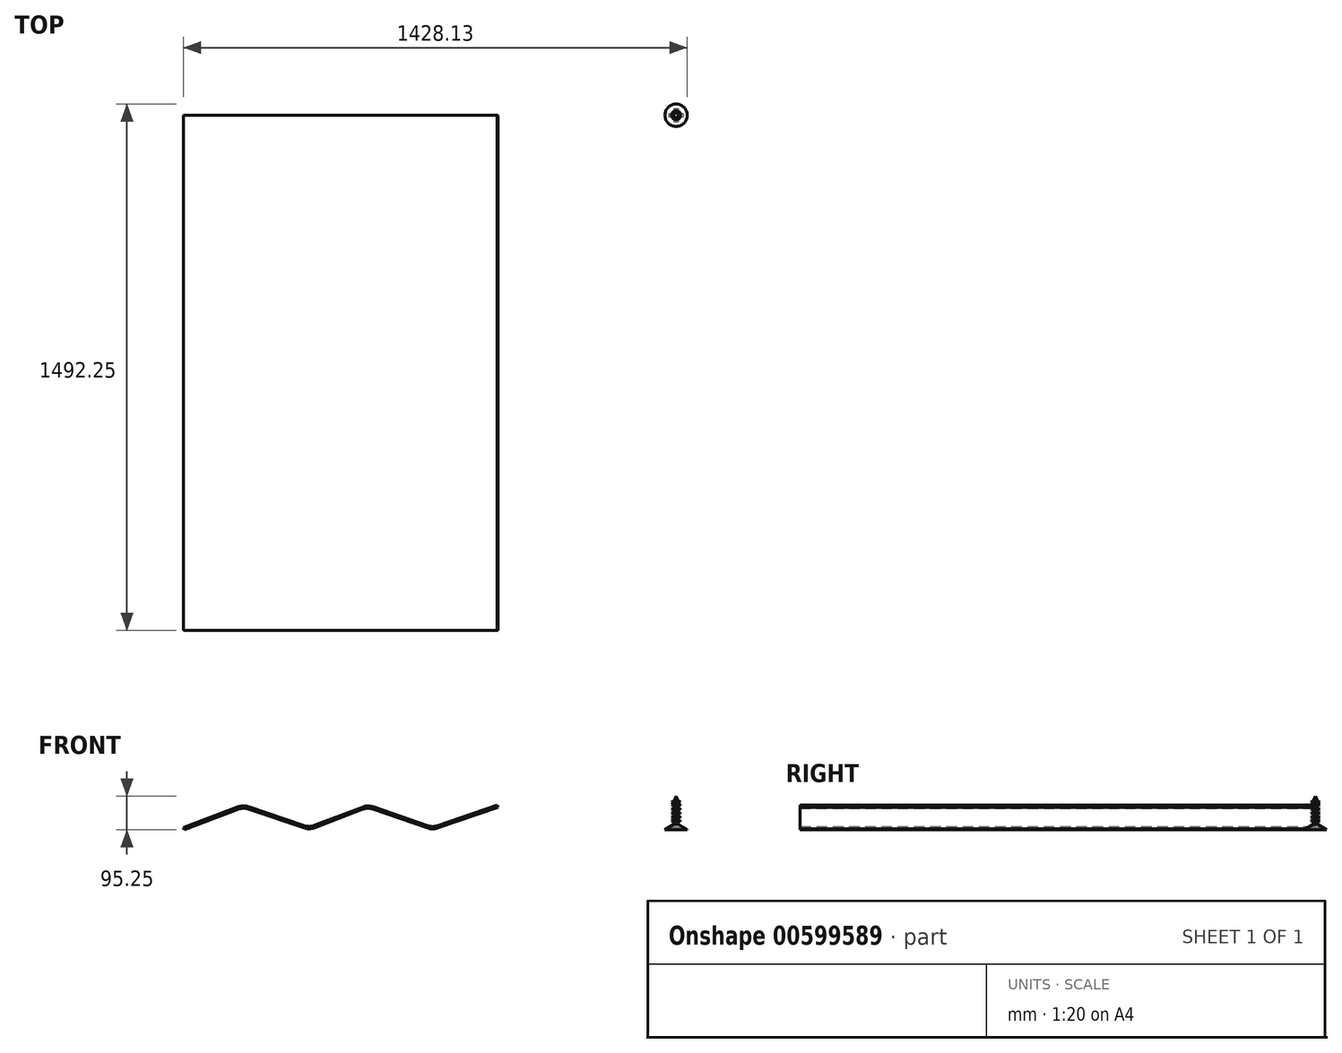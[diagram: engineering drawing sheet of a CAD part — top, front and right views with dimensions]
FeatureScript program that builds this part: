
annotation { "Feature Type Name" : "Feature", "Feature Type Description" : "" }
export const myFeature = defineFeature(function(context is Context, id is Id, definition is map)
    precondition{}
    {
        {
            var Q0;
            Q0=qCreatedBy(makeId("Front.planeOp"),FACE);
            var sketch = newSketch(context, id + "F0", { "sketchPlane" : qUnion([Q0])});
            skLineSegment(sketch, "E0", {"start": v(-278.83, 0) * mm, "end": v(-248.09, 11.64) * mm});
            skLineSegment(sketch, "E1", {"start": v(-242.43, 11.73) * mm, "end": v(-210.73, 0.97) * mm});
            skLineSegment(sketch, "E2", {"start": v(-205.03, 1.08) * mm, "end": v(-177.55, 11.6) * mm});
            skLineSegment(sketch, "E3", {"start": v(-171.8, 11.7) * mm, "end": v(-140.78, 0.95) * mm});
            skLineSegment(sketch, "E4", {"start": v(-135.32, 0.94) * mm, "end": v(-101.03, 12.7) * mm});
            skPoint(sketch, "E5.visualSharp", {"position": v(-245.28, 12.7) * mm});
            skArc(sketch, "E5.filletArc", {"start": v(-242.43, 11.73) * mm, "mid": v(-245.27, 12.18) * mm, "end": v(-248.09, 11.64) * mm});
            skPoint(sketch, "E6.visualSharp", {"position": v(-174.7, 12.7) * mm});
            skArc(sketch, "E6.filletArc", {"start": v(-171.8, 11.7) * mm, "mid": v(-174.69, 12.16) * mm, "end": v(-177.55, 11.6) * mm});
            skPoint(sketch, "E7.visualSharp", {"position": v(-138.05, 0) * mm});
            skArc(sketch, "E7.filletArc", {"start": v(-140.78, 0.95) * mm, "mid": v(-138.05, 0.48) * mm, "end": v(-135.32, 0.94) * mm});
            skPoint(sketch, "E8.visualSharp", {"position": v(-207.86, 0) * mm});
            skArc(sketch, "E8.filletArc", {"start": v(-210.73, 0.97) * mm, "mid": v(-207.87, 0.53) * mm, "end": v(-205.03, 1.08) * mm});
            skLineSegment(sketch, "E9.0", {"start": v(-135.32, 2.28) * mm, "end": v(-101.44, 13.9) * mm});
            skLineSegment(sketch, "E9.1", {"start": v(-171.4, 12.9) * mm, "end": v(-140.78, 2.29) * mm});
            skArc(sketch, "E9.2", {"start": v(-171.4, 12.9) * mm, "mid": v(-174.7, 13.43) * mm, "end": v(-178, 12.8) * mm});
            skLineSegment(sketch, "E9.3", {"start": v(-279.28, 1.19) * mm, "end": v(-248.54, 12.82) * mm});
            skArc(sketch, "E9.4", {"start": v(-242.02, 12.94) * mm, "mid": v(-245.29, 13.45) * mm, "end": v(-248.54, 12.82) * mm});
            skLineSegment(sketch, "E9.5", {"start": v(-242.02, 12.94) * mm, "end": v(-210.75, 2.32) * mm});
            skLineSegment(sketch, "E9.6", {"start": v(-205.06, 2.43) * mm, "end": v(-178, 12.8) * mm});
            skPoint(sketch, "E10.visualSharp", {"position": v(-207.89, 1.35) * mm});
            skArc(sketch, "E10.filletArc", {"start": v(-210.75, 2.32) * mm, "mid": v(-207.9, 1.88) * mm, "end": v(-205.06, 2.43) * mm});
            skPoint(sketch, "E11.visualSharp", {"position": v(-138.05, 1.34) * mm});
            skArc(sketch, "E11.filletArc", {"start": v(-140.78, 2.29) * mm, "mid": v(-138.05, 1.83) * mm, "end": v(-135.32, 2.28) * mm});
            skLineSegment(sketch, "E12", {"start": v(-101.03, 12.7) * mm, "end": v(-101.44, 13.9) * mm});
            skLineSegment(sketch, "E13", {"start": v(-278.83, 0) * mm, "end": v(-279.28, 1.19) * mm});
            skSolve(sketch);
        }
        {
            var Q0;
            Q0 = qSketchRegion(id + "F0", true);
            extrude(context, id + "F1", {"entities" : qUnion([Q0]), "depth" : 292.1 * mm, "offsetDistance" : 25.4 * mm});
        }
        {
            var Q0;
            Q0=qCreatedBy(makeId("Front.planeOp"),FACE);
            var sketch = newSketch(context, id + "F2", { "sketchPlane" : qUnion([Q0])});
            skLineSegment(sketch, "E14", {"start": v(0, 0) * mm, "end": v(-6.35, 0) * mm});
            skLineSegment(sketch, "E15", {"start": v(-6.35, 0) * mm, "end": v(-1.27, 2.96) * mm});
            skLineSegment(sketch, "E16", {"start": v(-1.27, 16.26) * mm, "end": v(0, 19.05) * mm});
            skLineSegment(sketch, "E17", {"start": v(-1.27, 2.96) * mm, "end": v(-1.27, 4.5) * mm});
            skLineSegment(sketch, "E18", {"start": v(-1.27, 4.5) * mm, "end": v(-2.54, 4.95) * mm});
            skLineSegment(sketch, "E19", {"start": v(-2.54, 4.95) * mm, "end": v(-1.27, 5.37) * mm});
            skLineSegment(sketch, "E20", {"start": v(-1.27, 5.37) * mm, "end": v(-1.27, 6.75) * mm});
            skLineSegment(sketch, "E21", {"start": v(-1.27, 6.75) * mm, "end": v(-2.54, 7.2) * mm});
            skLineSegment(sketch, "E22", {"start": v(-2.54, 7.2) * mm, "end": v(-1.27, 7.63) * mm});
            skLineSegment(sketch, "E23", {"start": v(-1.27, 7.63) * mm, "end": v(-1.27, 8.98) * mm});
            skLineSegment(sketch, "E24", {"start": v(-1.27, 8.98) * mm, "end": v(-2.54, 9.5) * mm});
            skLineSegment(sketch, "E25", {"start": v(-2.54, 9.5) * mm, "end": v(-1.27, 9.92) * mm});
            skLineSegment(sketch, "E26", {"start": v(-1.27, 9.92) * mm, "end": v(-1.27, 11.34) * mm});
            skLineSegment(sketch, "E27", {"start": v(-1.27, 11.34) * mm, "end": v(-2.54, 11.76) * mm});
            skLineSegment(sketch, "E28", {"start": v(-2.54, 11.76) * mm, "end": v(-1.27, 12.18) * mm});
            skLineSegment(sketch, "E29", {"start": v(-1.27, 12.18) * mm, "end": v(-1.27, 13.64) * mm});
            skLineSegment(sketch, "E30", {"start": v(-1.27, 13.64) * mm, "end": v(-2.54, 14.1) * mm});
            skLineSegment(sketch, "E31", {"start": v(-2.54, 14.1) * mm, "end": v(-1.27, 14.52) * mm});
            skLineSegment(sketch, "E32", {"start": v(-1.27, 14.52) * mm, "end": v(-1.27, 15.38) * mm});
            skLineSegment(sketch, "E33", {"start": v(-1.27, 15.38) * mm, "end": v(-2.54, 15.76) * mm});
            skLineSegment(sketch, "E34", {"start": v(-2.54, 15.76) * mm, "end": v(-1.27, 16.26) * mm});
            skPoint(sketch, "E35", {"position": v(-1.27, 10.63) * mm});
            skLineSegment(sketch, "E36", {"start": v(-3.4, 10.63) * mm, "end": v(3.08, 10.63) * mm, "construction": true});
            skLineSegment(sketch, "E37", {"start": v(0, 19.05) * mm, "end": v(0, 0) * mm});
            skSolve(sketch);
        }
        {
            var Q0;
            Q0=makeQuery(id+"F2.imprint","IMPRINT",FACE,{"disambiguationData":[TD([[makeQuery(id+"F2.imprint","IMPRINT",EDGE,{"derivedFrom":sQuery(id+"F2.wireOp",EDGE,"E14")}),-1.0]])]});
            var Q1;
            Q1=sQuery(id+"F2.wireOp",EDGE,"E37");
            revolve(context, id + "F3", {"entities" : qUnion([Q0]), "axis" : qUnion([Q1]), "revolveType" : RevolveType.FULL});
        }
        {
            var Q0;
            Q0=makeQuery(id+"F3.opRevolve","SWEPT_FACE",FACE,{"disambiguationData":[OSD([sQuery(id+"F2.wireOp",EDGE,"E14")])]});
            var sketch = newSketch(context, id + "F4", { "sketchPlane" : qUnion([Q0])});
            skLineSegment(sketch, "E38", {"start": v(-1.04, 3.9) * mm, "end": v(-1.04, 1.01) * mm});
            skLineSegment(sketch, "E39", {"start": v(-1.04, 1.01) * mm, "end": v(-3.87, 1.01) * mm});
            skLineSegment(sketch, "E40", {"start": v(-3.87, 1.01) * mm, "end": v(-3.87, -1.01) * mm});
            skLineSegment(sketch, "E41", {"start": v(-3.87, -1.01) * mm, "end": v(-1.04, -1.01) * mm});
            skLineSegment(sketch, "E42", {"start": v(-1.04, -1.01) * mm, "end": v(-1.04, -3.9) * mm});
            skLineSegment(sketch, "E43", {"start": v(-1.04, -3.9) * mm, "end": v(1.04, -3.9) * mm});
            skLineSegment(sketch, "E44", {"start": v(1.04, -3.9) * mm, "end": v(1.04, -1.01) * mm});
            skLineSegment(sketch, "E45", {"start": v(1.04, -1.01) * mm, "end": v(3.87, -1.01) * mm});
            skLineSegment(sketch, "E46", {"start": v(3.87, -1.01) * mm, "end": v(3.87, 1.01) * mm});
            skLineSegment(sketch, "E47", {"start": v(3.87, 1.01) * mm, "end": v(1.04, 1.01) * mm});
            skLineSegment(sketch, "E48", {"start": v(1.04, 1.01) * mm, "end": v(1.04, 3.9) * mm});
            skLineSegment(sketch, "E49", {"start": v(1.04, 3.9) * mm, "end": v(-1.04, 3.9) * mm});
            skLineSegment(sketch, "E50", {"start": v(-7.36, 0) * mm, "end": v(7.8, 0) * mm, "construction": true});
            skLineSegment(sketch, "E51", {"start": v(0, 8.09) * mm, "end": v(0, -9.13) * mm, "construction": true});
            skSolve(sketch);
        }
        {
            var Q0;
            Q0=makeQuery(id+"F4.imprint","IMPRINT",FACE,{"disambiguationData":[TD([[makeQuery(id+"F4.imprint","IMPRINT",EDGE,{"derivedFrom":sQuery(id+"F4.wireOp",EDGE,"E38")}),1.0]])]});
            extrude(context, id + "F5", {"entities" : qUnion([Q0]), "operationType" : NewBodyOperationType.REMOVE, "oppositeDirection" : true, "depth" : 1.27 * mm, "offsetDistance" : 25.4 * mm});
        }
        {
            var Q0;
            Q0=makeQuery(id+"F1.opExtrude","SWEPT_BODY",BODY,{"disambiguationData":[OSD([sQuery(id+"F0.wireOp",EDGE,"E0"),sQuery(id+"F0.wireOp",EDGE,"E1"),sQuery(id+"F0.wireOp",EDGE,"E2"),sQuery(id+"F0.wireOp",EDGE,"E3"),sQuery(id+"F0.wireOp",EDGE,"E4"),sQuery(id+"F0.wireOp",EDGE,"E5.filletArc"),sQuery(id+"F0.wireOp",EDGE,"E6.filletArc"),sQuery(id+"F0.wireOp",EDGE,"E7.filletArc"),sQuery(id+"F0.wireOp",EDGE,"E8.filletArc"),sQuery(id+"F0.wireOp",EDGE,"E9.0"),sQuery(id+"F0.wireOp",EDGE,"E9.1"),sQuery(id+"F0.wireOp",EDGE,"E9.2"),sQuery(id+"F0.wireOp",EDGE,"E9.3"),sQuery(id+"F0.wireOp",EDGE,"E9.4"),sQuery(id+"F0.wireOp",EDGE,"E9.5"),sQuery(id+"F0.wireOp",EDGE,"E9.6"),sQuery(id+"F0.wireOp",EDGE,"E10.filletArc"),sQuery(id+"F0.wireOp",EDGE,"E11.filletArc"),sQuery(id+"F0.wireOp",EDGE,"E12"),sQuery(id+"F0.wireOp",EDGE,"E13")])]});
            var Q1;
            Q1=makeQuery(id+"F3.opRevolve","SWEPT_BODY",BODY,{"disambiguationData":[OSD([sQuery(id+"F2.wireOp",EDGE,"E14"),sQuery(id+"F2.wireOp",EDGE,"E15"),sQuery(id+"F2.wireOp",EDGE,"E16"),sQuery(id+"F2.wireOp",EDGE,"E17"),sQuery(id+"F2.wireOp",EDGE,"E18"),sQuery(id+"F2.wireOp",EDGE,"E19"),sQuery(id+"F2.wireOp",EDGE,"E20"),sQuery(id+"F2.wireOp",EDGE,"E21"),sQuery(id+"F2.wireOp",EDGE,"E22"),sQuery(id+"F2.wireOp",EDGE,"E23"),sQuery(id+"F2.wireOp",EDGE,"E24"),sQuery(id+"F2.wireOp",EDGE,"E25"),sQuery(id+"F2.wireOp",EDGE,"E26"),sQuery(id+"F2.wireOp",EDGE,"E27"),sQuery(id+"F2.wireOp",EDGE,"E28"),sQuery(id+"F2.wireOp",EDGE,"E29"),sQuery(id+"F2.wireOp",EDGE,"E30"),sQuery(id+"F2.wireOp",EDGE,"E31"),sQuery(id+"F2.wireOp",EDGE,"E32"),sQuery(id+"F2.wireOp",EDGE,"E33"),sQuery(id+"F2.wireOp",EDGE,"E34"),sQuery(id+"F2.wireOp",EDGE,"E37")])]});
            var Q2;
            Q2=qCreatedBy(makeId("Origin.pointOp"),VERTEX);
            transform(context, id + "F6", {"entities" : qUnion([Q0, Q1]), "transformType" : TransformType.SCALE_UNIFORMLY, "scale" : 5, "scalePoint" : qUnion([Q2]), "makeCopy" : false});
        }
    });
